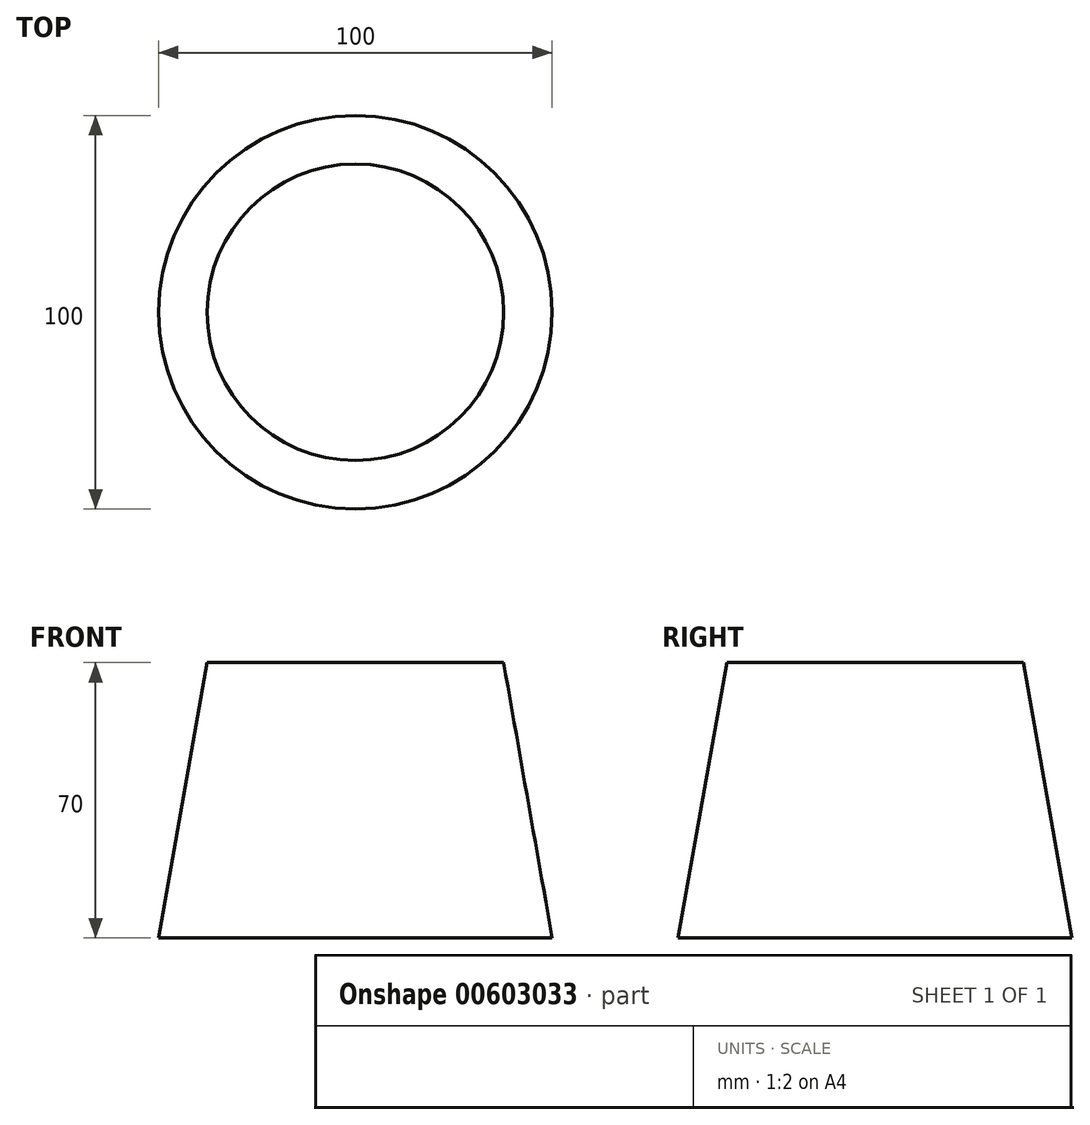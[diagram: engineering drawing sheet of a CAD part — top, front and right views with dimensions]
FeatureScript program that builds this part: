
annotation { "Feature Type Name" : "Feature", "Feature Type Description" : "" }
export const myFeature = defineFeature(function(context is Context, id is Id, definition is map)
    precondition{}
    {
        {
            var Q0;
            Q0=qCreatedBy(makeId("Top.planeOp"),FACE);
            var sketch = newSketch(context, id + "F0", { "sketchPlane" : qUnion([Q0])});
            skCircle(sketch, "E0", {"center": v(0, 0) * mm, "radius": 50 * mm});
            skSolve(sketch);
        }
        {
            var Q0;
            Q0 = qSketchRegion(id + "F0", true);
            extrude(context, id + "F1", {"entities" : qUnion([Q0]), "depth" : 70 * mm, "offsetDistance" : 25 * mm, "hasDraft" : true, "draftAngle" : 10 * degree, "draftPullDirection" : true});
        }
    });
